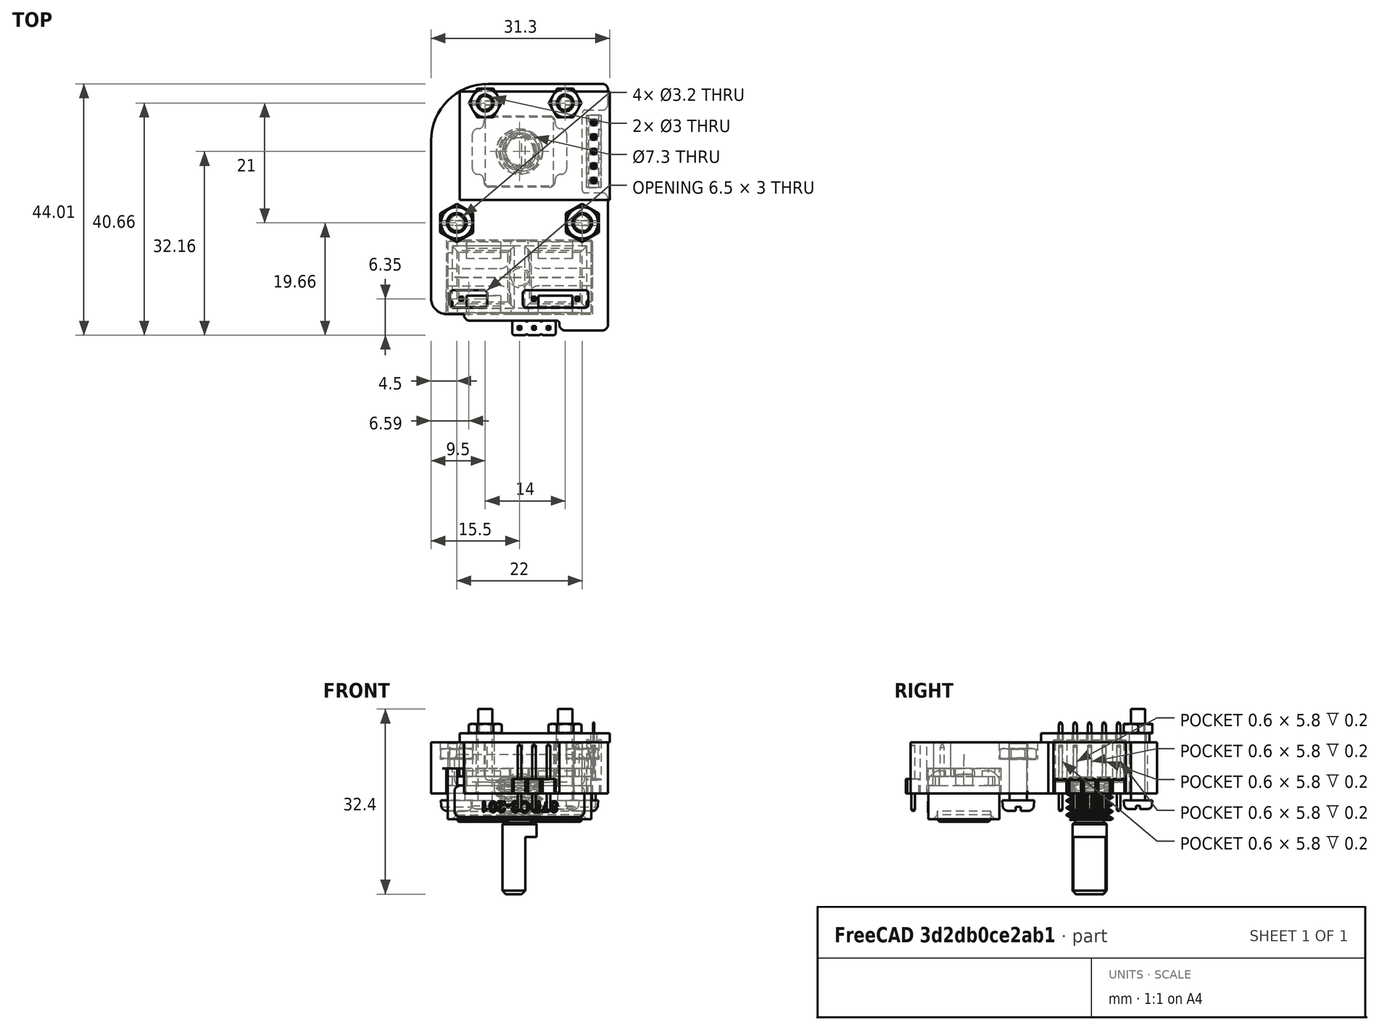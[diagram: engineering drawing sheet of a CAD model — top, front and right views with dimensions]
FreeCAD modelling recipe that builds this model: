
FCSTD DOCUMENT  (FreeCAD 0.18.4R)
Label: MJ_3d_holder_right_3p-r2-asm
License: All rights reserved
LicenseURL: http://en.wikipedia.org/wiki/All_rights_reserved
objects: Sketcher::SketchObject×17, PartDesign::Pad×9, PartDesign::Pocket×8, Part::Feature×8, Part::FeaturePython×8, PartDesign::Fillet×6, PartDesign::Body×6, PartDesign::Chamfer×4, PartDesign::Plane×2, Part::Compound×2, App::DocumentObjectGroup×2, PartDesign::FeatureBase×1, Part::Part2DObjectPython×1, Part::Extrusion×1
note: 90 computed .brp shape members not serialized (recipe doc carries the construction recipe); baked Part::Feature solids carry a one-line shape summary decoded from their .brp

FEATURE [Sketcher::SketchObject] Sketch  label="Sketch_body_outline"
  MapMode = 5
  Support = -> [XY_Plane]
  sketch-geometry (59):
    g0: Circle CenterX=0 CenterY=0 CenterZ=0 NormalX=0 NormalY=0 NormalZ=1 AngleXU=0 Radius=3.65
    g1: Circle CenterX=-11 CenterY=-12.5 CenterZ=0 NormalX=0 NormalY=0 NormalZ=1 AngleXU=0 Radius=1.6
    g2: Circle CenterX=11 CenterY=-12.5 CenterZ=0 NormalX=0 NormalY=0 NormalZ=1 AngleXU=0 Radius=1.6
    g3: Circle CenterX=-6 CenterY=8.5 CenterZ=0 NormalX=0 NormalY=0 NormalZ=1 AngleXU=0 Radius=1.6
    g4: Circle CenterX=8 CenterY=8.5 CenterZ=0 NormalX=0 NormalY=0 NormalZ=1 AngleXU=0 Radius=1.6
    g5: LineSegment [constr] StartX=11 StartY=7.25 StartZ=0 EndX=15 EndY=7.25 EndZ=0
    g6: LineSegment [constr] StartX=15 StartY=7.25 StartZ=0 EndX=15 EndY=-7.25 EndZ=0
    g7: LineSegment [constr] StartX=15 StartY=-7.25 StartZ=0 EndX=11 EndY=-7.25 EndZ=0
    g8: LineSegment [constr] StartX=11 StartY=-7.25 StartZ=0 EndX=11 EndY=7.25 EndZ=0
    g9: GeomPoint X=13 Y=-7.25 Z=0
    g10: GeomPoint X=0 Y=-22 Z=0
    g11: LineSegment [constr] StartX=-12.7 StartY=-15.65 StartZ=0 EndX=12.7 EndY=-15.65 EndZ=0
    g12: LineSegment [constr] StartX=12.7 StartY=-15.65 StartZ=0 EndX=12.7 EndY=-28.35 EndZ=0
    g13: LineSegment [constr] StartX=12.7 StartY=-28.35 StartZ=0 EndX=-12.7 EndY=-28.35 EndZ=0
    g14: LineSegment [constr] StartX=-12.7 StartY=-28.35 StartZ=0 EndX=-12.7 EndY=-15.65 EndZ=0
    g15: LineSegment StartX=15.5 StartY=-31.35 StartZ=0 EndX=15.5 EndY=-7.25 EndZ=0
    g16: LineSegment StartX=15.5 StartY=11.85 StartZ=0 EndX=-5.5 EndY=11.85 EndZ=0
    g17: LineSegment StartX=-15.5 StartY=1.85 StartZ=0 EndX=-15.5 EndY=-25.7 EndZ=0
    g18: LineSegment [constr] StartX=-7 StartY=-29.62 StartZ=0 EndX=7 EndY=-29.62 EndZ=0
    g19: LineSegment [constr] StartX=7 StartY=-29.62 StartZ=0 EndX=7 EndY=-32.16 EndZ=0
    g20: LineSegment [constr] StartX=7 StartY=-32.16 StartZ=0 EndX=-7 EndY=-32.16 EndZ=0
    g21: LineSegment [constr] StartX=-7 StartY=-32.16 StartZ=0 EndX=-7 EndY=-29.62 EndZ=0
    g22: GeomPoint X=-7 Y=-30.89 Z=0
    g23: LineSegment [constr] StartX=-6 StartY=6 StartZ=0 EndX=6 EndY=6 EndZ=0
    g24: LineSegment [constr] StartX=6 StartY=6 StartZ=0 EndX=6 EndY=-6 EndZ=0
    g25: LineSegment [constr] StartX=6 StartY=-6 StartZ=0 EndX=-6 EndY=-6 EndZ=0
    g26: LineSegment [constr] StartX=-6 StartY=-6 StartZ=0 EndX=-6 EndY=6 EndZ=0
    g27: LineSegment [constr] StartX=-10.5 StartY=10.5 StartZ=0 EndX=15.8 EndY=10.5 EndZ=0
    g28: LineSegment [constr] StartX=15.8 StartY=10.5 StartZ=0 EndX=15.8 EndY=-8.5 EndZ=0
    g29: LineSegment [constr] StartX=15.8 StartY=-8.5 StartZ=0 EndX=-10.5 EndY=-8.5 EndZ=0
    g30: LineSegment [constr] StartX=-10.5 StartY=-8.5 StartZ=0 EndX=-10.5 EndY=10.5 EndZ=0
    g31: LineSegment StartX=11 StartY=7.25 StartZ=0 EndX=15.5 EndY=7.25 EndZ=0
    g32: LineSegment StartX=15.5 StartY=-7.25 StartZ=0 EndX=11 EndY=-7.25 EndZ=0
    g33: LineSegment StartX=11 StartY=-7.25 StartZ=0 EndX=11 EndY=7.25 EndZ=0
    g34: LineSegment StartX=15.5 StartY=7.25 StartZ=0 EndX=15.5 EndY=11.85 EndZ=0
    g35: LineSegment StartX=7 StartY=-29.62 StartZ=0 EndX=7 EndY=-31.35 EndZ=0
    g36: LineSegment StartX=7 StartY=-31.35 StartZ=0 EndX=15.5 EndY=-31.35 EndZ=0
    g37: Circle [constr] CenterX=-10.16 CenterY=-25.81 CenterZ=0 NormalX=0 NormalY=0 NormalZ=1 AngleXU=0 Radius=0.5
    g38: Circle [constr] CenterX=2.54 CenterY=-25.81 CenterZ=0 NormalX=0 NormalY=0 NormalZ=1 AngleXU=0 Radius=0.5
    g39: Circle [constr] CenterX=10.16 CenterY=-25.81 CenterZ=0 NormalX=0 NormalY=0 NormalZ=1 AngleXU=0 Radius=0.5
    g40: LineSegment StartX=-5.66 StartY=-24.31 StartZ=0 EndX=-12.16 EndY=-24.31 EndZ=0
    g41: LineSegment StartX=-12.16 StartY=-24.31 StartZ=0 EndX=-12.16 EndY=-27.31 EndZ=0
    g42: LineSegment StartX=-12.16 StartY=-27.31 StartZ=0 EndX=-5.66 EndY=-27.31 EndZ=0
    g43: LineSegment StartX=-5.66 StartY=-27.31 StartZ=0 EndX=-5.66 EndY=-24.31 EndZ=0
    g44: LineSegment StartX=0.6 StartY=-24.31 StartZ=0 EndX=12.1 EndY=-24.31 EndZ=0
    g45: LineSegment StartX=12.1 StartY=-24.31 StartZ=0 EndX=12.1 EndY=-27.31 EndZ=0
    g46: LineSegment StartX=12.1 StartY=-27.31 StartZ=0 EndX=0.6 EndY=-27.31 EndZ=0
    g47: LineSegment StartX=0.6 StartY=-27.31 StartZ=0 EndX=0.6 EndY=-24.31 EndZ=0
    g48: GeomPoint X=6.35 Y=-25.81 Z=0
    g49: ArcOfCircle CenterX=-12.7 CenterY=-25.7 CenterZ=0 NormalX=0 NormalY=0 NormalZ=1 AngleXU=0 Radius=2.8 StartAngle=3.14159 EndAngle=4.71239
    g50: LineSegment StartX=-9.7 StartY=-29.62 StartZ=0 EndX=7 EndY=-29.62 EndZ=0
    g51: LineSegment StartX=-9.7 StartY=-29.62 StartZ=0 EndX=-9.7 EndY=-28.5 EndZ=0
    g52: LineSegment StartX=-9.7 StartY=-28.5 StartZ=0 EndX=-12.7 EndY=-28.5 EndZ=0
    g53: Circle [constr] CenterX=0 CenterY=-30.89 CenterZ=0 NormalX=0 NormalY=0 NormalZ=1 AngleXU=0 Radius=0.5
    g54: Circle [constr] CenterX=2.54 CenterY=-30.89 CenterZ=0 NormalX=0 NormalY=0 NormalZ=1 AngleXU=0 Radius=0.5
    g55: Circle [constr] CenterX=5.08 CenterY=-30.89 CenterZ=0 NormalX=0 NormalY=0 NormalZ=1 AngleXU=0 Radius=0.5
    g56: ArcOfCircle CenterX=-5.5 CenterY=1.85 CenterZ=0 NormalX=0 NormalY=0 NormalZ=1 AngleXU=0 Radius=10 StartAngle=1.5708 EndAngle=3.14159
    g57: GeomPoint X=-15.5 Y=-12.5 Z=0
    g58: GeomPoint X=15.5 Y=-12.5 Z=0
  constraints (157):
    c: Coincident(g0,g-1)
    c: Diameter(g0) = 7.3
    c: Diameter(g2) = 3.2
    c: Equal(g1,g2)
    c: DistanceY(g2,g-1) = 12.5
    c: DistanceX(g1,g2) = 22
    c: Symmetric(g1,g2,g-2)
    c: Horizontal(g3,g4)
    c: Equal(g2,g4)
    c: Equal(g4,g3)
    c: DistanceY(g-1,g3) = 8.5
    c: DistanceX(g3,g4) = 14
    c: DistanceX(g3,g-1) = 6
    c: Coincident(g5,g6)
    c: Coincident(g6,g7)
    c: Coincident(g7,g8)
    c: Coincident(g8,g5)
    c: Horizontal(g5)
    c: Horizontal(g7)
    c: Vertical(g8)
    c: DistanceX(g5,g5) = 4
    c: DistanceY(g6,g6) = 14.5
    c: Symmetric(g5,g6,g-1)
    c: DistanceX(g-1,g9) = 13
    c: Symmetric(g7,g6,g9)
    c: PointOnObject(g10,g-2)
    c: DistanceY(g10,g0) = 22
    c: Coincident(g11,g12)
    c: Coincident(g12,g13)
    c: Coincident(g13,g14)
    c: Coincident(g14,g11)
    c: Horizontal(g11)
    c: Vertical(g12)
    c: Vertical(g14)
    c: DistanceX(g13,g13) = 25.4
    c: DistanceY(g12,g12) = 12.7
    c: Horizontal(g13)
    c: Symmetric(g11,g12,g10)
    c: Coincident(g36,g15)
    c: Coincident(g34,g16)
    c: Vertical(g15)
    c: Vertical(g17)
    c: DistanceY(g36,g12) = 3
    c: Coincident(g18,g19)
    c: Coincident(g19,g20)
    c: Coincident(g20,g21)
    c: Coincident(g21,g18)
    c: Vertical(g19)
    c: Vertical(g21)
    c: DistanceY(g19,g19) = 2.54
    c: DistanceX(g18,g18) = 14
    c: DistanceY(g22,g13) = 2.54
    c: Symmetric(g18,g20,g22)
    c: Coincident(g23,g24)
    c: Coincident(g24,g25)
    c: Coincident(g25,g26)
    c: Coincident(g26,g23)
    c: Horizontal(g23)
    c: Horizontal(g25)
    c: Vertical(g24)
    c: Vertical(g26)
    c: DistanceX(g23,g23) = 12
    c: Equal(g24,g23)
    c: Symmetric(g23,g24,g0)
    c: Coincident(g27,g28)
    c: Coincident(g28,g29)
    c: Coincident(g29,g30)
    c: Coincident(g30,g27)
    c: Horizontal(g27)
    c: Horizontal(g29)
    c: Vertical(g28)
    c: Vertical(g30)
    c: DistanceY(g28,g28) = 19
    c: DistanceX(g27,g27) = 26.3
    c: DistanceX(g27,g-1) = 10.5
    c: DistanceY(g-1,g27) = 10.5
    c: Coincident(g32,g33)
    c: Coincident(g33,g31)
    c: Horizontal(g31)
    c: Horizontal(g32)
    c: Vertical(g33)
    c: Coincident(g31,g5)
    c: Equal(g6,g33)
    c: Tangent(g15,g34)
    c: Vertical(g35)
    c: PointOnObject(g36,g19)
    c: Coincident(g32,g15)
    c: Coincident(g31,g34)
    c: Horizontal(g39,g38)
    c: Horizontal(g38,g37)
    c: Equal(g39,g38)
    c: Equal(g38,g37)
    c: Diameter(g37) = 1
    c: DistanceY(g37,g10) = 3.81
    c: DistanceX(g38,g39) = 7.62
    c: DistanceX(g10,g38) = 2.54
    c: DistanceX(g37,g-1) = 10.16
    c: Coincident(g40,g41)
    c: Coincident(g41,g42)
    c: Coincident(g42,g43)
    c: Coincident(g43,g40)
    c: Horizontal(g40)
    c: Horizontal(g42)
    c: Vertical(g41)
    c: Vertical(g43)
    c: Coincident(g44,g45)
    c: Coincident(g45,g46)
    c: Coincident(g46,g47)
    c: Coincident(g47,g44)
    c: Horizontal(g44)
    c: Horizontal(g46)
    c: Vertical(g45)
    c: Vertical(g47)
    c: Equal(g47,g43)
    c: DistanceY(g45,g45) = 3
    c: Symmetric(g38,g39,g48)
    c: Symmetric(g44,g45,g48)
    c: Horizontal(g44,g40)
    c: DistanceX(g46,g46) = 11.5
    c: DistanceX(g42,g42) = 6.5
    c: DistanceX(g40,g37) = 2
    c: DistanceY(g34,g34) = 4.6
    c: Tangent(g17,g49) = -1.5708
    c: Horizontal(g35,g18)
    c: Coincident(g35,g36)
    c: Symmetric(g20,g19,g-2)
    c: Horizontal(g18)
    c: PointOnObject(g50,g18)
    c: Coincident(g50,g35)
    c: Horizontal(g36)
    c: Vertical(g49,g49)
    c: Coincident(g51,g50)
    c: Vertical(g51)
    c: DistanceY(g51,g51) = 1.12
    c: Coincident(g52,g51)
    c: Horizontal(g52)
    c: DistanceX(g52,g52) = 3
    c: Coincident(g49,g52)
    c: Radius(g49) = 2.8
    c: PointOnObject(g53,g-2)
    c: Equal(g38,g53)
    c: Equal(g53,g54)
    c: Equal(g54,g55)
    c: Horizontal(g53,g54)
    c: Horizontal(g54,g55)
    c: DistanceX(g53,g54) = 2.54
    c: DistanceX(g54,g55) = 2.54
    c: DistanceY(g54,g38) = 5.08
    c: DistanceX(g17,g15) = 31
    c: Tangent(g17,g56) = -1.5708
    c: Tangent(g16,g56) = -1.5708
    c: Radius(g56) = 10
    c: Horizontal(g16)
    c: PointOnObject(g57,g17)
    c: PointOnObject(g58,g15)
    c: Horizontal(g2,g58)
    c: Symmetric(g57,g58,g-2)
FEATURE [PartDesign::Pad] Pad  label="BodyPad"
  Length = 9
  Length2 = 100
  Profile = -> Sketch
  Type = 0
FEATURE [Sketcher::SketchObject] Sketch002  label="Sketch_rotary_7mm_pocket"
  MapMode = 5
  Placement = pos=(0,0,9) rot=(0,0,1;0rad)
  Support = -> [Pad]
  sketch-geometry (12):
    g0: LineSegment StartX=8.25 StartY=-4 StartZ=0 EndX=6.25 EndY=-4 EndZ=0
    g1: LineSegment StartX=-8.25 StartY=-4 StartZ=0 EndX=-8.25 EndY=4 EndZ=0
    g2: LineSegment StartX=-8.25 StartY=4 StartZ=0 EndX=-6.25 EndY=4 EndZ=0
    g3: LineSegment StartX=8.25 StartY=4 StartZ=0 EndX=8.25 EndY=-4 EndZ=0
    g4: LineSegment StartX=-6.25 StartY=6.25 StartZ=0 EndX=6.25 EndY=6.25 EndZ=0
    g5: LineSegment StartX=6.25 StartY=6.25 StartZ=0 EndX=6.25 EndY=4 EndZ=0
    g6: LineSegment StartX=6.25 StartY=-6.25 StartZ=0 EndX=-6.25 EndY=-6.25 EndZ=0
    g7: LineSegment StartX=-6.25 StartY=-6.25 StartZ=0 EndX=-6.25 EndY=-4 EndZ=0
    g8: LineSegment StartX=6.25 StartY=4 StartZ=0 EndX=8.25 EndY=4 EndZ=0
    g9: LineSegment StartX=-6.25 StartY=-4 StartZ=0 EndX=-8.25 EndY=-4 EndZ=0
    g10: LineSegment StartX=-6.25 StartY=4 StartZ=0 EndX=-6.25 EndY=6.25 EndZ=0
    g11: LineSegment StartX=6.25 StartY=-4 StartZ=0 EndX=6.25 EndY=-6.25 EndZ=0
  constraints (30):
    c: Coincident(g9,g1)
    c: Coincident(g1,g2)
    c: Coincident(g8,g3)
    c: Coincident(g3,g0)
    c: Horizontal(g0)
    c: Horizontal(g2)
    c: Vertical(g1)
    c: Vertical(g3)
    c: DistanceX(g2,g8) = 16.5
    c: DistanceY(g1,g1) = 8
    c: Symmetric(g0,g1,g-1)
    c: Coincident(g4,g5)
    c: Coincident(g11,g6)
    c: Coincident(g6,g7)
    c: Coincident(g10,g4)
    c: Horizontal(g4)
    c: Horizontal(g6)
    c: Vertical(g5)
    c: Vertical(g7)
    c: DistanceX(g4,g4) = 12.5
    c: DistanceY(g7,g10) = 12.5
    c: Symmetric(g4,g11,g-1)
    c: Tangent(g2,g8)
    c: Tangent(g0,g9)
    c: Coincident(g7,g9)
    c: Coincident(g10,g2)
    c: Tangent(g7,g10)
    c: Coincident(g5,g8)
    c: Coincident(g11,g0)
    c: Tangent(g5,g11)
FEATURE [PartDesign::Pocket] Pocket  label="RotaryPocket"
  BaseFeature = -> Pad
  Length = 7
  Length2 = 100
  Profile = -> Sketch002
  Type = 0
FEATURE [Sketcher::SketchObject] Sketch001  label="Sketch_hexnut_3mm_pockets"
  MapMode = 5
  Placement = pos=(0,0,9) rot=(0,0,1;0rad)
  Support = -> [Pocket]
  sketch-geometry (14):
    g0: LineSegment StartX=-8.1 StartY=-14.1743 StartZ=0 EndX=-8.1 EndY=-10.8257 EndZ=0
    g1: LineSegment StartX=-8.1 StartY=-10.8257 StartZ=0 EndX=-11 EndY=-9.15137 EndZ=0
    g2: LineSegment StartX=-11 StartY=-9.15137 StartZ=0 EndX=-13.9 EndY=-10.8257 EndZ=0
    g3: LineSegment StartX=-13.9 StartY=-10.8257 StartZ=0 EndX=-13.9 EndY=-14.1743 EndZ=0
    g4: LineSegment StartX=-13.9 StartY=-14.1743 StartZ=0 EndX=-11 EndY=-15.8486 EndZ=0
    g5: LineSegment StartX=-11 StartY=-15.8486 StartZ=0 EndX=-8.1 EndY=-14.1743 EndZ=0
    g6: Circle [constr] CenterX=-11 CenterY=-12.5 CenterZ=0 NormalX=0 NormalY=0 NormalZ=1 AngleXU=0 Radius=3.34863
    g7: LineSegment StartX=13.9 StartY=-14.1743 StartZ=0 EndX=13.9 EndY=-10.8257 EndZ=0
    g8: LineSegment StartX=13.9 StartY=-10.8257 StartZ=0 EndX=11 EndY=-9.15137 EndZ=0
    g9: LineSegment StartX=11 StartY=-9.15137 StartZ=0 EndX=8.1 EndY=-10.8257 EndZ=0
    g10: LineSegment StartX=8.1 StartY=-10.8257 StartZ=0 EndX=8.1 EndY=-14.1743 EndZ=0
    g11: LineSegment StartX=8.1 StartY=-14.1743 StartZ=0 EndX=11 EndY=-15.8486 EndZ=0
    g12: LineSegment StartX=11 StartY=-15.8486 StartZ=0 EndX=13.9 EndY=-14.1743 EndZ=0
    g13: Circle [constr] CenterX=11 CenterY=-12.5 CenterZ=0 NormalX=0 NormalY=0 NormalZ=1 AngleXU=0 Radius=3.34863
  constraints (33):
    c: Coincident(g0,g1)
    c: Coincident(g1,g2)
    c: Coincident(g2,g3)
    c: Coincident(g3,g4)
    c: Coincident(g4,g5)
    c: Coincident(g5,g0)
    c: Equal(g0, g1-g5) x5
    c: PointOnObject(g0,g6)
    c: PointOnObject(g1,g6)
    c: PointOnObject(g2,g6)
    c: PointOnObject(g3,g6)
    c: PointOnObject(g4,g6)
    c: PointOnObject(g5,g6)
    c: Coincident(g7,g8)
    c: Coincident(g8,g9)
    c: Coincident(g9,g10)
    c: Coincident(g10,g11)
    c: Coincident(g11,g12)
    c: Coincident(g12,g7)
    c: Equal(g7, g8-g12) x5
    c: PointOnObject(g7,g13)
    c: PointOnObject(g8,g13)
    c: PointOnObject(g9,g13)
    c: PointOnObject(g10,g13)
    c: PointOnObject(g11,g13)
    c: PointOnObject(g12,g13)
    c: DistanceX(g6,g13) = 22
    c: Symmetric(g6,g13,g-2)
    c: DistanceY(g6,g-1) = 12.5
    c: DistanceX(g3,g0) = 5.8
    c: Vertical(g3)
    c: DistanceX(g10,g7) = 5.8
    c: Vertical(g7)
FEATURE [PartDesign::Pocket] Pocket001
  BaseFeature = -> Pocket
  Length = 3
  Length2 = 100
  Profile = -> Sketch001
  Type = 0
FEATURE [Sketcher::SketchObject] Sketch003  label="Sketch_Grayhill_3mm_pocket"
  MapMode = 5
  Placement = pos=(0,0,0) rot=(1,0,0;3.14159rad)
  Support = -> [Pocket001]
  sketch-geometry (5):
    g0: LineSegment StartX=12.85 StartY=15.5 StartZ=0 EndX=-12.85 EndY=15.5 EndZ=0
    g1: LineSegment StartX=-12.85 StartY=15.5 StartZ=0 EndX=-12.85 EndY=28.5 EndZ=0
    g2: LineSegment StartX=-12.85 StartY=28.5 StartZ=0 EndX=12.85 EndY=28.5 EndZ=0
    g3: LineSegment StartX=12.85 StartY=28.5 StartZ=0 EndX=12.85 EndY=15.5 EndZ=0
    g4: GeomPoint X=0 Y=22 Z=0
  constraints (13):
    c: Coincident(g0,g1)
    c: Coincident(g1,g2)
    c: Coincident(g2,g3)
    c: Coincident(g3,g0)
    c: Horizontal(g0)
    c: Horizontal(g2)
    c: Vertical(g1)
    c: Vertical(g3)
    c: DistanceX(g2,g2) = 25.7
    c: DistanceY(g3,g3) = 13
    c: PointOnObject(g4,g-2)
    c: DistanceY(g-1,g4) = 22
    c: Symmetric(g0,g1,g4)
FEATURE [PartDesign::Pocket] Pocket002
  BaseFeature = -> Pocket001
  Length = 3
  Length2 = 100
  Profile = -> Sketch003
  Type = 0
FEATURE [Sketcher::SketchObject] Sketch004  label="Sketch_Grayhill_1_4mm_pocket"
  MapMode = 5
  Placement = pos=(0,0,3) rot=(1,0,0;3.14159rad)
  Support = -> [Pocket002]
  sketch-geometry (34):
    g0: LineSegment [constr] StartX=12.85 StartY=15.5 StartZ=0 EndX=-12.85 EndY=15.5 EndZ=0
    g1: LineSegment [constr] StartX=-12.85 StartY=15.5 StartZ=0 EndX=-12.85 EndY=28.5 EndZ=0
    g2: LineSegment [constr] StartX=-12.85 StartY=28.5 StartZ=0 EndX=12.85 EndY=28.5 EndZ=0
    g3: LineSegment [constr] StartX=12.85 StartY=28.5 StartZ=0 EndX=12.85 EndY=15.5 EndZ=0
    g4: GeomPoint X=0 Y=22 Z=0
    g5: LineSegment [constr] StartX=12.85 StartY=20.5 StartZ=0 EndX=-12.85 EndY=20.5 EndZ=0
    g6: LineSegment [constr] StartX=-12.85 StartY=20.5 StartZ=0 EndX=-12.85 EndY=23.5 EndZ=0
    g7: LineSegment [constr] StartX=-12.85 StartY=23.5 StartZ=0 EndX=12.85 EndY=23.5 EndZ=0
    g8: LineSegment [constr] StartX=12.85 StartY=23.5 StartZ=0 EndX=12.85 EndY=20.5 EndZ=0
    g9: LineSegment [constr] StartX=1.5 StartY=15.5 StartZ=0 EndX=-1.5 EndY=15.5 EndZ=0
    g10: LineSegment [constr] StartX=-1.5 StartY=15.5 StartZ=0 EndX=-1.5 EndY=28.5 EndZ=0
    g11: LineSegment [constr] StartX=-1.5 StartY=28.5 StartZ=0 EndX=1.5 EndY=28.5 EndZ=0
    g12: LineSegment [constr] StartX=1.5 StartY=28.5 StartZ=0 EndX=1.5 EndY=15.5 EndZ=0
    g13: Circle CenterX=0 CenterY=22 CenterZ=0 NormalX=0 NormalY=0 NormalZ=1 AngleXU=0 Radius=1.8
    g14: LineSegment StartX=1.5 StartY=15.5 StartZ=0 EndX=12.85 EndY=15.5 EndZ=0
    g15: LineSegment StartX=12.85 StartY=15.5 StartZ=0 EndX=12.85 EndY=20.5 EndZ=0
    g16: LineSegment StartX=12.85 StartY=20.5 StartZ=0 EndX=3.5 EndY=20.5 EndZ=0
    g17: LineSegment StartX=1.5 StartY=18.5 StartZ=0 EndX=1.5 EndY=15.5 EndZ=0
    g18: LineSegment StartX=-1.5 StartY=15.5 StartZ=0 EndX=-12.85 EndY=15.5 EndZ=0
    g19: LineSegment StartX=-12.85 StartY=15.5 StartZ=0 EndX=-12.85 EndY=20.5 EndZ=0
    g20: LineSegment StartX=-12.85 StartY=20.5 StartZ=0 EndX=-3.5 EndY=20.5 EndZ=0
    g21: LineSegment StartX=-1.5 StartY=18.5 StartZ=0 EndX=-1.5 EndY=15.5 EndZ=0
    g22: LineSegment StartX=12.85 StartY=23.5 StartZ=0 EndX=3.5 EndY=23.5 EndZ=0
    g23: LineSegment StartX=1.5 StartY=25.5 StartZ=0 EndX=1.5 EndY=28.5 EndZ=0
    g24: LineSegment StartX=1.5 StartY=28.5 StartZ=0 EndX=12.85 EndY=28.5 EndZ=0
    g25: LineSegment StartX=12.85 StartY=28.5 StartZ=0 EndX=12.85 EndY=23.5 EndZ=0
    g26: LineSegment StartX=-12.85 StartY=23.5 StartZ=0 EndX=-3.5 EndY=23.5 EndZ=0
    g27: LineSegment StartX=-1.5 StartY=25.5 StartZ=0 EndX=-1.5 EndY=28.5 EndZ=0
    g28: LineSegment StartX=-1.5 StartY=28.5 StartZ=0 EndX=-12.85 EndY=28.5 EndZ=0
    g29: LineSegment StartX=-12.85 StartY=28.5 StartZ=0 EndX=-12.85 EndY=23.5 EndZ=0
    g30: ArcOfCircle CenterX=3.5 CenterY=18.5 CenterZ=0 NormalX=0 NormalY=0 NormalZ=1 AngleXU=0 Radius=2 StartAngle=1.5708 EndAngle=3.14159
    g31: ArcOfCircle CenterX=-3.5 CenterY=18.5 CenterZ=0 NormalX=0 NormalY=0 NormalZ=1 AngleXU=0 Radius=2 StartAngle=-9e-16 EndAngle=1.5708
    g32: ArcOfCircle CenterX=-3.5 CenterY=25.5 CenterZ=0 NormalX=0 NormalY=0 NormalZ=1 AngleXU=0 Radius=2 StartAngle=4.71239 EndAngle=6.28319
    g33: ArcOfCircle CenterX=3.5 CenterY=25.5 CenterZ=0 NormalX=0 NormalY=0 NormalZ=1 AngleXU=0 Radius=2 StartAngle=3.14159 EndAngle=4.71239
  constraints (85):
    c: Coincident(g0,g1)
    c: Coincident(g1,g2)
    c: Coincident(g2,g3)
    c: Coincident(g3,g0)
    c: Horizontal(g0)
    c: Horizontal(g2)
    c: Vertical(g1)
    c: Vertical(g3)
    c: DistanceX(g0,g0) = 25.7
    c: DistanceY(g3,g3) = 13
    c: PointOnObject(g4,g-2)
    c: DistanceY(g-1,g4) = 22
    c: Symmetric(g0,g1,g4)
    c: Coincident(g5,g6)
    c: Coincident(g6,g7)
    c: Coincident(g7,g8)
    c: Coincident(g8,g5)
    c: Horizontal(g5)
    c: Horizontal(g7)
    c: Vertical(g6)
    c: Vertical(g8)
    c: PointOnObject(g5,g3)
    c: Symmetric(g5,g6,g4)
    c: DistanceY(g5,g7) = 3
    c: Coincident(g9,g10)
    c: Coincident(g10,g11)
    c: Coincident(g11,g12)
    c: Coincident(g12,g9)
    c: Horizontal(g9)
    c: Horizontal(g11)
    c: Vertical(g10)
    c: Vertical(g12)
    c: PointOnObject(g9,g0)
    c: Symmetric(g9,g10,g4)
    c: DistanceX(g10,g11) = 3
    c: Coincident(g13,g4)
    c: Diameter(g13) = 3.6
    c: Coincident(g14,g15)
    c: Coincident(g15,g16)
    c: Coincident(g17,g14)
    c: Horizontal(g14)
    c: Horizontal(g16)
    c: Vertical(g15)
    c: Vertical(g17)
    c: Coincident(g14,g9)
    c: Coincident(g15,g5)
    c: Coincident(g18,g19)
    c: Coincident(g19,g20)
    c: Coincident(g21,g18)
    c: Horizontal(g18)
    c: Horizontal(g20)
    c: Vertical(g19)
    c: Vertical(g21)
    c: Coincident(g18,g9)
    c: Coincident(g19,g5)
    c: Coincident(g23,g24)
    c: Coincident(g24,g25)
    c: Coincident(g25,g22)
    c: Horizontal(g22)
    c: Horizontal(g24)
    c: Vertical(g23)
    c: Vertical(g25)
    c: Coincident(g22,g7)
    c: Coincident(g23,g11)
    c: Coincident(g27,g28)
    c: Coincident(g28,g29)
    c: Coincident(g29,g26)
    c: Horizontal(g26)
    c: Horizontal(g28)
    c: Vertical(g27)
    c: Vertical(g29)
    c: Coincident(g26,g6)
    c: Coincident(g27,g10)
    c: Tangent(g17,g30) = -1.5708
    c: Tangent(g16,g30) = -1.5708
    c: Tangent(g21,g31) = 1.5708
    c: Tangent(g20,g31) = 1.5708
    c: Tangent(g26,g32) = -1.5708
    c: Tangent(g27,g32) = -1.5708
    c: Tangent(g22,g33) = 1.5708
    c: Tangent(g23,g33) = 1.5708
    c: Radius(g30) = 2
    c: Equal(g30,g31)
    c: Equal(g31,g32)
    c: Equal(g32,g33)
FEATURE [PartDesign::Pocket] Pocket003
  BaseFeature = -> Pocket002
  Length = 1.4
  Length2 = 100
  Profile = -> Sketch004
  Type = 0
FEATURE [PartDesign::Fillet] Fillet
  Base = -> Pocket003 [Edge85,Edge10,Edge1,Edge107,Edge104,Edge103]
  BaseFeature = -> Pocket003
  Radius = 1
FEATURE [PartDesign::Fillet] Fillet001
  Base = -> Fillet [Edge151,Edge147,Edge143,Edge135,Edge149,Edge153,Edge145,Edge133,Edge137,Edge141,Edge132,Edge139]
  BaseFeature = -> Fillet
  Radius = 0.99
FEATURE [PartDesign::Fillet] Fillet002
  Base = -> Fillet001 [Edge153,Edge150,Edge117,Edge281,Edge284,Edge269,Edge173,Edge267,Edge230,Edge170,Edge176,Edge180,Edge166,Edge175,Edge165,Edge285,Edge256,Edge168,Edge178,Edge214,Edge215,Edge161,Edge163,Edge133]
  BaseFeature = -> Fillet001
  Radius = 0.5
FEATURE [PartDesign::Body] Body  label="3d_holder_right-r2"
  Group = -> [Sketch004,Sketch,Pad,Sketch001,Sketch002,Sketch003,Pocket,Pocket001,Pocket002,Pocket003,Fillet,Fillet001,Fillet002]
  Origin = -> Origin
  Tip = -> Fillet002
FEATURE [Sketcher::SketchObject] Sketch012
  MapMode = 5
  Placement = pos=(0,0,0) rot=(1,0,0;1.5708rad)
  Support = -> [XZ_Plane003]
  sketch-geometry (12):
    g0: LineSegment StartX=-11.725 StartY=5.425 StartZ=0 EndX=11.725 EndY=5.425 EndZ=0
    g1: LineSegment StartX=11.725 StartY=5.425 StartZ=0 EndX=11.725 EndY=4.275 EndZ=0
    g2: LineSegment StartX=11.725 StartY=4.275 StartZ=0 EndX=12.575 EndY=4.275 EndZ=0
    g3: LineSegment StartX=12.575 StartY=4.275 StartZ=0 EndX=12.575 EndY=-4.275 EndZ=0
    g4: LineSegment StartX=12.575 StartY=-4.275 StartZ=0 EndX=11.725 EndY=-4.275 EndZ=0
    g5: LineSegment StartX=11.725 StartY=-4.275 StartZ=0 EndX=11.725 EndY=-5.425 EndZ=0
    g6: LineSegment StartX=11.725 StartY=-5.425 StartZ=0 EndX=-11.725 EndY=-5.425 EndZ=0
    g7: LineSegment StartX=-11.725 StartY=-5.425 StartZ=0 EndX=-11.725 EndY=-4.275 EndZ=0
    g8: LineSegment StartX=-11.725 StartY=-4.275 StartZ=0 EndX=-12.575 EndY=-4.275 EndZ=0
    g9: LineSegment StartX=-12.575 StartY=-4.275 StartZ=0 EndX=-12.575 EndY=4.275 EndZ=0
    g10: LineSegment StartX=-12.575 StartY=4.275 StartZ=0 EndX=-11.725 EndY=4.275 EndZ=0
    g11: LineSegment StartX=-11.725 StartY=4.275 StartZ=0 EndX=-11.725 EndY=5.425 EndZ=0
  constraints (34):
    c: Horizontal(g0)
    c: Coincident(g0,g1)
    c: Vertical(g1)
    c: Coincident(g1,g2)
    c: Horizontal(g2)
    c: Coincident(g2,g3)
    c: Vertical(g3)
    c: Coincident(g3,g4)
    c: Horizontal(g4)
    c: Coincident(g4,g5)
    c: Vertical(g5)
    c: Coincident(g5,g6)
    c: Coincident(g6,g7)
    c: Vertical(g7)
    c: Coincident(g7,g8)
    c: Horizontal(g8)
    c: Coincident(g8,g9)
    c: Coincident(g9,g10)
    c: Coincident(g10,g11)
    c: Coincident(g11,g0)
    c: Equal(g11,g1)
    c: Equal(g1,g5)
    c: Equal(g5,g7)
    c: Equal(g2,g4)
    c: Equal(g4,g8)
    c: Equal(g8,g10)
    c: Equal(g3,g9)
    c: Equal(g0,g6)
    c: DistanceX(g9,g2) = 25.15
    c: DistanceY(g5,g0) = 10.85
    c: DistanceX(g10,g10) = 0.85
    c: DistanceY(g11,g11) = 1.15
    c: Symmetric(g6,g6,g-2)
    c: Symmetric(g9,g9,g-1)
FEATURE [PartDesign::Pad] Pad008  label="PCBPad"
  Length = 1.6
  Length2 = 100
  Placement = pos=(0,0,0) rot=(1,0,0;1.5708rad)
  Profile = -> Sketch012
  Reversed = true
  Type = 0
FEATURE [Part::Feature] Part__Feature001  label="BTN_A-Brass_pin-5.75mm"
  Placement = pos=(12.7,0,0) rot=(0,0,1;0rad)
  shape: bbox 0.7 x 5.75 x 0.7 mm, 14 faces (baked)
FEATURE [Sketcher::SketchObject] Sketch013
  MapMode = 5
  Placement = pos=(0,0,0) rot=(1,0,0;1.5708rad)
  Support = -> [XZ_Plane004]
  sketch-geometry (4):
    g0: LineSegment StartX=-12.575 StartY=6.225 StartZ=0 EndX=12.575 EndY=6.225 EndZ=0
    g1: LineSegment StartX=12.575 StartY=6.225 StartZ=0 EndX=12.575 EndY=-6.225 EndZ=0
    g2: LineSegment StartX=12.575 StartY=-6.225 StartZ=0 EndX=-12.575 EndY=-6.225 EndZ=0
    g3: LineSegment StartX=-12.575 StartY=-6.225 StartZ=0 EndX=-12.575 EndY=6.225 EndZ=0
  constraints (10):
    c: Coincident(g0,g1)
    c: Coincident(g1,g2)
    c: Coincident(g2,g3)
    c: Coincident(g3,g0)
    c: Horizontal(g2)
    c: Vertical(g1)
    c: DistanceX(g0,g0) = 25.15
    c: DistanceY(g3,g3) = 12.45
    c: Symmetric(g0,g0,g-2)
    c: Symmetric(g2,g0,g-1)
FEATURE [PartDesign::Pad] Pad001
  Length = 5.9
  Length2 = 100
  Placement = pos=(0,0,0) rot=(1,0,0;1.5708rad)
  Profile = -> Sketch013
  Type = 0
FEATURE [Sketcher::SketchObject] Sketch018
  MapMode = 5
  Placement = pos=(0,-5.9,1.3e-15) rot=(1,0,0;1.5708rad)
  Support = -> [Pad001]
  sketch-geometry (11):
    g0: LineSegment StartX=-11 StartY=4.65 StartZ=0 EndX=-1.7 EndY=4.65 EndZ=0
    g1: LineSegment StartX=-1.7 StartY=4.65 StartZ=0 EndX=-1.7 EndY=-4.65 EndZ=0
    g2: LineSegment StartX=-1.7 StartY=-4.65 StartZ=0 EndX=-11 EndY=-4.65 EndZ=0
    g3: LineSegment StartX=-11 StartY=-4.65 StartZ=0 EndX=-11 EndY=4.65 EndZ=0
    g4: LineSegment [constr] StartX=-6.35 StartY=4.65 StartZ=0 EndX=-6.35 EndY=-4.65 EndZ=0
    g5: LineSegment StartX=1.7 StartY=4.65 StartZ=0 EndX=11 EndY=4.65 EndZ=0
    g6: LineSegment StartX=11 StartY=4.65 StartZ=0 EndX=11 EndY=-4.65 EndZ=0
    g7: LineSegment StartX=11 StartY=-4.65 StartZ=0 EndX=1.7 EndY=-4.65 EndZ=0
    g8: LineSegment StartX=1.7 StartY=-4.65 StartZ=0 EndX=1.7 EndY=4.65 EndZ=0
    g9: LineSegment [constr] StartX=6.35 StartY=4.65 StartZ=0 EndX=6.35 EndY=-4.65 EndZ=0
    g10: LineSegment [constr] StartX=-11 StartY=4.65 StartZ=0 EndX=1.7 EndY=4.65 EndZ=0
  constraints (31):
    c: Coincident(g0,g1)
    c: Coincident(g1,g2)
    c: Coincident(g2,g3)
    c: Coincident(g3,g0)
    c: Horizontal(g0)
    c: Horizontal(g2)
    c: Vertical(g1)
    c: DistanceY(g3,g3) = 9.3
    c: DistanceX(g0,g0) = 9.3
    c: Symmetric(g0,g2,g-1)
    c: PointOnObject(g4,g0)
    c: PointOnObject(g4,g2)
    c: Symmetric(g0,g0,g4)
    c: DistanceX(g4,g-1) = 6.35
    c: Coincident(g5,g6)
    c: Coincident(g6,g7)
    c: Coincident(g7,g8)
    c: Coincident(g8,g5)
    c: Horizontal(g5)
    c: Horizontal(g7)
    c: Vertical(g6)
    c: Equal(g3,g8) = 9.3
    c: Equal(g0,g5) = 9.3
    c: PointOnObject(g9,g5)
    c: PointOnObject(g9,g7)
    c: Symmetric(g5,g5,g9)
    c: Coincident(g0,g10)
    c: Coincident(g5,g10)
    c: Distance(g10) = 12.7
    c: Horizontal(g10)
    c: Vertical(g8)
FEATURE [PartDesign::Pocket] Pocket008
  BaseFeature = -> Pad001
  Length = 1.4
  Length2 = 100
  Placement = pos=(0,0,0) rot=(1,0,0;1.5708rad)
  Profile = -> Sketch018
  Type = 0
FEATURE [PartDesign::Chamfer] Chamfer
  Base = -> Pocket008 [Edge17,Edge20,Edge19,Edge18,Edge16,Edge13,Edge14,Edge15]
  BaseFeature = -> Pocket008
  Placement = pos=(0,0,0) rot=(1,0,0;1.5708rad)
  Size = 0.8
FEATURE [PartDesign::Plane] DatumPlane
  Length = 29.6355
  MapMode = 5
  Placement = pos=(0,-4.5,3.4e-15) rot=(1,0,0;1.5708rad)
  ResizeMode = 0
  Support = -> [Chamfer]
  Width = 24.4855
FEATURE [Sketcher::SketchObject] Sketch011  label="SketchRightBtn"
  MapMode = 5
  Placement = pos=(0,-4.5,3.4e-15) rot=(1,0,0;1.5708rad)
  Support = -> [DatumPlane]
  sketch-geometry (5):
    g0: LineSegment StartX=1.7 StartY=4.65 StartZ=0 EndX=11 EndY=4.65 EndZ=0
    g1: LineSegment StartX=11 StartY=4.65 StartZ=0 EndX=11 EndY=-4.65 EndZ=0
    g2: LineSegment StartX=11 StartY=-4.65 StartZ=0 EndX=1.7 EndY=-4.65 EndZ=0
    g3: LineSegment StartX=1.7 StartY=-4.65 StartZ=0 EndX=1.7 EndY=4.65 EndZ=0
    g4: LineSegment [constr] StartX=6.35 StartY=4.65 StartZ=0 EndX=6.35 EndY=-4.65 EndZ=0
  constraints (14):
    c: Coincident(g0,g1)
    c: Coincident(g1,g2)
    c: Coincident(g2,g3)
    c: Coincident(g3,g0)
    c: Horizontal(g0)
    c: Horizontal(g2)
    c: Vertical(g1)
    c: DistanceY(g3,g3) = 9.3
    c: DistanceX(g0,g0) = 9.3
    c: Symmetric(g0,g2,g-1)
    c: PointOnObject(g4,g0)
    c: PointOnObject(g4,g2)
    c: Symmetric(g0,g0,g4)
    c: DistanceX(g4,g-1) = -6.35
FEATURE [PartDesign::Pad] Pad002
  Length = 1.8
  Length2 = 100
  Placement = pos=(0,-4.5,5e-15) rot=(1,0,0;1.5708rad)
  Profile = -> Sketch011
  Type = 0
FEATURE [Sketcher::SketchObject] Sketch015
  ExternalGeometry = -> [Chamfer]
  MapMode = 5
  Placement = pos=(0,0,0) rot=(-1,0,0;1.5708rad)
  Support = -> [Chamfer]
  sketch-geometry (24):
    g0: LineSegment StartX=12.575 StartY=-4.315 StartZ=0 EndX=12.575 EndY=-6.225 EndZ=0
    g1: LineSegment StartX=12.575 StartY=-6.225 StartZ=0 EndX=10.945 EndY=-6.225 EndZ=0
    g2: LineSegment StartX=10.945 StartY=-6.225 StartZ=0 EndX=10.945 EndY=-5.425 EndZ=0
    g3: LineSegment StartX=10.945 StartY=-5.425 StartZ=0 EndX=11.775 EndY=-5.425 EndZ=0
    g4: LineSegment StartX=11.775 StartY=-5.425 StartZ=0 EndX=11.775 EndY=-4.315 EndZ=0
    g5: LineSegment StartX=11.775 StartY=-4.315 StartZ=0 EndX=12.575 EndY=-4.315 EndZ=0
    g6: LineSegment StartX=-10.945 StartY=-6.225 StartZ=0 EndX=-12.575 EndY=-6.225 EndZ=0
    g7: LineSegment StartX=-12.575 StartY=-6.225 StartZ=0 EndX=-12.575 EndY=-4.315 EndZ=0
    g8: LineSegment StartX=-12.575 StartY=-4.315 StartZ=0 EndX=-11.775 EndY=-4.315 EndZ=0
    g9: LineSegment StartX=-11.775 StartY=-4.315 StartZ=0 EndX=-11.775 EndY=-5.425 EndZ=0
    g10: LineSegment StartX=-11.775 StartY=-5.425 StartZ=0 EndX=-10.945 EndY=-5.425 EndZ=0
    g11: LineSegment StartX=-10.945 StartY=-5.425 StartZ=0 EndX=-10.945 EndY=-6.225 EndZ=0
    g12: LineSegment StartX=12.575 StartY=4.315 StartZ=0 EndX=12.575 EndY=6.225 EndZ=0
    g13: LineSegment StartX=12.575 StartY=6.225 StartZ=0 EndX=10.945 EndY=6.225 EndZ=0
    g14: LineSegment StartX=10.945 StartY=6.225 StartZ=0 EndX=10.945 EndY=5.425 EndZ=0
    g15: LineSegment StartX=10.945 StartY=5.425 StartZ=0 EndX=11.775 EndY=5.425 EndZ=0
    g16: LineSegment StartX=11.775 StartY=5.425 StartZ=0 EndX=11.775 EndY=4.315 EndZ=0
    g17: LineSegment StartX=11.775 StartY=4.315 StartZ=0 EndX=12.575 EndY=4.315 EndZ=0
    g18: LineSegment StartX=-11.775 StartY=4.315 StartZ=0 EndX=-11.775 EndY=5.425 EndZ=0
    g19: LineSegment StartX=-11.775 StartY=5.425 StartZ=0 EndX=-10.945 EndY=5.425 EndZ=0
    g20: LineSegment StartX=-10.945 StartY=5.425 StartZ=0 EndX=-10.945 EndY=6.225 EndZ=0
    g21: LineSegment StartX=-10.945 StartY=6.225 StartZ=0 EndX=-12.575 EndY=6.225 EndZ=0
    g22: LineSegment StartX=-12.575 StartY=6.225 StartZ=0 EndX=-12.575 EndY=4.315 EndZ=0
    g23: LineSegment StartX=-12.575 StartY=4.315 StartZ=0 EndX=-11.775 EndY=4.315 EndZ=0
  constraints (68):
    c: Vertical(g0)
    c: Coincident(g0,g1)
    c: Horizontal(g1)
    c: Coincident(g1,g2)
    c: Vertical(g2)
    c: Coincident(g2,g3)
    c: Horizontal(g3)
    c: Coincident(g3,g4)
    c: Vertical(g4)
    c: Coincident(g4,g5)
    c: Coincident(g5,g0)
    c: Horizontal(g5)
    c: DistanceX(g1,g1) = 1.63
    c: DistanceY(g0,g0) = 1.91
    c: DistanceY(g2,g2) = 0.8
    c: DistanceX(g5,g5) = 0.8
    c: Horizontal(g6)
    c: Coincident(g6,g7)
    c: Vertical(g7)
    c: Coincident(g7,g8)
    c: Horizontal(g8)
    c: Coincident(g8,g9)
    c: Vertical(g9)
    c: Coincident(g9,g10)
    c: Horizontal(g10)
    c: Coincident(g10,g11)
    c: Coincident(g11,g6)
    c: Vertical(g11)
    c: Equal(g6,g1)
    c: Equal(g7,g0)
    c: Equal(g8,g5)
    c: Equal(g11,g2)
    c: Vertical(g12)
    c: Coincident(g12,g13)
    c: Horizontal(g13)
    c: Coincident(g13,g14)
    c: Vertical(g14)
    c: Coincident(g14,g15)
    c: Horizontal(g15)
    c: Coincident(g15,g16)
    c: Vertical(g16)
    c: Coincident(g16,g17)
    c: Horizontal(g17)
    c: Vertical(g18)
    c: Coincident(g18,g19)
    c: Horizontal(g19)
    c: Coincident(g19,g20)
    c: Vertical(g20)
    c: Coincident(g20,g21)
    c: Horizontal(g21)
    c: Coincident(g21,g22)
    c: Vertical(g22)
    c: Coincident(g22,g23)
    c: Coincident(g23,g18)
    c: Horizontal(g23)
    c: Equal(g23,g8)
    c: Equal(g17,g5)
    c: Equal(g14,g20)
    c: Equal(g14,g2)
    c: Equal(g12,g22)
    c: Equal(g21,g13)
    c: Equal(g12,g0)
    c: Equal(g13,g1)
    c: Coincident(g-3,g0)
    c: Coincident(g-4,g6)
    c: Coincident(g-5,g12)
    c: Coincident(g-6,g21)
    c: Coincident(g17,g12)
FEATURE [PartDesign::Pad] Pad003
  BaseFeature = -> Chamfer
  Length = 3
  Length2 = 100
  Placement = pos=(0,0,0) rot=(1,0,0;1.5708rad)
  Profile = -> Sketch015
  Type = 0
FEATURE [Sketcher::SketchObject] Sketch007
  ExternalGeometry = -> [Chamfer]
  MapMode = 5
  Placement = pos=(0,0,0) rot=(-1,0,0;1.5708rad)
  Support = -> [Pad003]
  sketch-geometry (24):
    g0: LineSegment StartX=-9.2875 StartY=6.225 StartZ=0 EndX=-3.2875 EndY=6.225 EndZ=0
    g1: LineSegment StartX=-3.2875 StartY=6.225 StartZ=0 EndX=-3.2875 EndY=3.225 EndZ=0
    g2: LineSegment StartX=-3.2875 StartY=3.225 StartZ=0 EndX=-9.2875 EndY=3.225 EndZ=0
    g3: LineSegment StartX=-9.2875 StartY=3.225 StartZ=0 EndX=-9.2875 EndY=6.225 EndZ=0
    g4: LineSegment [constr] StartX=-12.575 StartY=6.225 StartZ=0 EndX=12.575 EndY=6.225 EndZ=0
    g5: LineSegment [constr] StartX=-12.575 StartY=-6.225 StartZ=0 EndX=12.575 EndY=-6.225 EndZ=0
    g6: GeomPoint X=1e-16 Y=6.225 Z=0
    g7: GeomPoint X=4e-16 Y=-6.225 Z=0
    g8: GeomPoint X=-6.2875 Y=-6.225 Z=0
    g9: GeomPoint X=6.2875 Y=-6.225 Z=0
    g10: GeomPoint X=-6.2875 Y=6.225 Z=0
    g11: GeomPoint X=6.2875 Y=6.225 Z=0
    g12: LineSegment StartX=3.2875 StartY=6.225 StartZ=0 EndX=9.2875 EndY=6.225 EndZ=0
    g13: LineSegment StartX=9.2875 StartY=6.225 StartZ=0 EndX=9.2875 EndY=3.225 EndZ=0
    g14: LineSegment StartX=9.2875 StartY=3.225 StartZ=0 EndX=3.2875 EndY=3.225 EndZ=0
    g15: LineSegment StartX=3.2875 StartY=3.225 StartZ=0 EndX=3.2875 EndY=6.225 EndZ=0
    g16: LineSegment StartX=-9.2875 StartY=-3.225 StartZ=0 EndX=-3.2875 EndY=-3.225 EndZ=0
    g17: LineSegment StartX=-3.2875 StartY=-3.225 StartZ=0 EndX=-3.2875 EndY=-6.225 EndZ=0
    g18: LineSegment StartX=-3.2875 StartY=-6.225 StartZ=0 EndX=-9.2875 EndY=-6.225 EndZ=0
    g19: LineSegment StartX=-9.2875 StartY=-6.225 StartZ=0 EndX=-9.2875 EndY=-3.225 EndZ=0
    g20: LineSegment StartX=3.2875 StartY=-3.225 StartZ=0 EndX=9.2875 EndY=-3.225 EndZ=0
    g21: LineSegment StartX=9.2875 StartY=-3.225 StartZ=0 EndX=9.2875 EndY=-6.225 EndZ=0
    g22: LineSegment StartX=9.2875 StartY=-6.225 StartZ=0 EndX=3.2875 EndY=-6.225 EndZ=0
    g23: LineSegment StartX=3.2875 StartY=-6.225 StartZ=0 EndX=3.2875 EndY=-3.225 EndZ=0
  constraints (54):
    c: Coincident(g0,g1)
    c: Coincident(g1,g2)
    c: Coincident(g2,g3)
    c: Coincident(g3,g0)
    c: Horizontal(g0)
    c: Horizontal(g2)
    c: Vertical(g1)
    c: Vertical(g3)
    c: DistanceX(g0,g0) = 6
    c: DistanceY(g1,g1) = 3
    c: Coincident(g4,g-3)
    c: Coincident(g4,g-4)
    c: Coincident(g5,g-6)
    c: Coincident(g5,g-5)
    c: Symmetric(g4,g4,g6)
    c: Symmetric(g5,g5,g7)
    c: Symmetric(g7,g5,g9)
    c: Symmetric(g5,g7,g8)
    c: Symmetric(g4,g6,g10)
    c: Symmetric(g6,g4,g11)
    c: Symmetric(g0,g0,g10)
    c: Coincident(g12,g13)
    c: Coincident(g13,g14)
    c: Coincident(g14,g15)
    c: Coincident(g15,g12)
    c: Horizontal(g12)
    c: Horizontal(g14)
    c: Vertical(g13)
    c: Vertical(g15)
    c: Coincident(g16,g17)
    c: Coincident(g17,g18)
    c: Coincident(g18,g19)
    c: Coincident(g19,g16)
    c: Horizontal(g16)
    c: Horizontal(g18)
    c: Vertical(g17)
    c: Vertical(g19)
    c: Coincident(g20,g21)
    c: Coincident(g21,g22)
    c: Coincident(g22,g23)
    c: Coincident(g23,g20)
    c: Horizontal(g20)
    c: Horizontal(g22)
    c: Vertical(g21)
    c: Vertical(g23)
    c: Equal(g12,g0)
    c: Equal(g20,g16)
    c: Equal(g16,g0)
    c: Equal(g17,g21)
    c: Equal(g21,g13)
    c: Equal(g13,g1)
    c: Symmetric(g18,g17,g8)
    c: Symmetric(g22,g21,g9)
    c: Symmetric(g12,g12,g11)
FEATURE [PartDesign::Pad] Pad004
  BaseFeature = -> Pad003
  Length = 2.6
  Length2 = 100
  Placement = pos=(0,0,0) rot=(1,0,0;1.5708rad)
  Profile = -> Sketch007
  Type = 0
FEATURE [Sketcher::SketchObject] Sketch008
  MapMode = 5
  Placement = pos=(0,0,0) rot=(-1,0,0;1.5708rad)
  Support = -> [Pad004]
  sketch-geometry (1):
    g0: Circle CenterX=0 CenterY=0 CenterZ=0 NormalX=0 NormalY=0 NormalZ=1 AngleXU=0 Radius=1.5
  constraints (2):
    c: Coincident(g0,g-1)
    c: Diameter(g0) = 3
FEATURE [Sketcher::SketchObject] Sketch016  label="SketchLeftBtn"
  MapMode = 5
  Placement = pos=(0,-4.5,3.4e-15) rot=(1,0,0;1.5708rad)
  Support = -> [DatumPlane]
  sketch-geometry (5):
    g0: LineSegment StartX=-11 StartY=4.65 StartZ=0 EndX=-1.7 EndY=4.65 EndZ=0
    g1: LineSegment StartX=-1.7 StartY=4.65 StartZ=0 EndX=-1.7 EndY=-4.65 EndZ=0
    g2: LineSegment StartX=-1.7 StartY=-4.65 StartZ=0 EndX=-11 EndY=-4.65 EndZ=0
    g3: LineSegment StartX=-11 StartY=-4.65 StartZ=0 EndX=-11 EndY=4.65 EndZ=0
    g4: LineSegment [constr] StartX=-6.35 StartY=4.65 StartZ=0 EndX=-6.35 EndY=-4.65 EndZ=0
  constraints (14):
    c: Coincident(g0,g1)
    c: Coincident(g1,g2)
    c: Coincident(g2,g3)
    c: Coincident(g3,g0)
    c: Horizontal(g0)
    c: Horizontal(g2)
    c: Vertical(g1)
    c: DistanceY(g3,g3) = 9.3
    c: DistanceX(g0,g0) = 9.3
    c: Symmetric(g0,g2,g-1)
    c: PointOnObject(g4,g0)
    c: PointOnObject(g4,g2)
    c: Symmetric(g0,g0,g4)
    c: DistanceX(g4,g-1) = 6.35
FEATURE [PartDesign::Pad] Pad006
  Length = 1.8
  Length2 = 100
  Placement = pos=(0,-4.5,5e-15) rot=(1,0,0;1.5708rad)
  Profile = -> Sketch016
  Type = 0
FEATURE [PartDesign::Chamfer] Chamfer001  label="BtnLeftChamfer"
  Base = -> Pad006 [Face6]
  BaseFeature = -> Pad006
  Placement = pos=(0,-4.5,5e-15) rot=(1,0,0;1.5708rad)
  Size = 0.35
FEATURE [PartDesign::Body] Body001  label="ButtonLeftBody"
  Group = -> [Sketch016,Pad006,Chamfer001]
  Origin = -> Origin001
  Tip = -> Chamfer001
FEATURE [PartDesign::Chamfer] Chamfer002  label="BtnRightChamfer"
  Base = -> Pad002 [Face6]
  BaseFeature = -> Pad002
  Placement = pos=(0,-4.5,5e-15) rot=(1,0,0;1.5708rad)
  Size = 0.35
FEATURE [PartDesign::Body] Body002  label="ButtonRightBody"
  Group = -> [Sketch011,Pad002,Chamfer002]
  Origin = -> Origin002
  Tip = -> Chamfer002
FEATURE [Part::Feature] Part__Feature  label="COMMON-Brass_pin-5.75mm"
  Placement = pos=(20.32,0,0) rot=(0,0,1;0rad)
  shape: bbox 0.7 x 5.75 x 0.7 mm, 14 faces (baked)
FEATURE [PartDesign::Body] Body003  label="PCBBody"
  Group = -> [Sketch012,Pad008]
  Origin = -> Origin003
  Tip = -> Pad008
FEATURE [Part::Feature] Part__Feature002  label="BTN_B-Brass_pin-5.75mm"
  shape: bbox 0.7 x 5.75 x 0.7 mm, 14 faces (baked)
FEATURE [PartDesign::Pad] Pad005
  BaseFeature = -> Pad004
  Length = 2
  Length2 = 100
  Placement = pos=(0,0,0) rot=(1,0,0;1.5708rad)
  Profile = -> Sketch008
  Type = 0
FEATURE [PartDesign::Fillet] Fillet004
  Base = -> Pad005 [Edge179]
  BaseFeature = -> Pad005
  Placement = pos=(0,0,0) rot=(1,0,0;1.5708rad)
  Radius = 0.5
FEATURE [PartDesign::Chamfer] Chamfer003
  Base = -> Fillet004 [Edge146,Edge147,Edge130,Edge129]
  BaseFeature = -> Fillet004
  Placement = pos=(0,0,0) rot=(1,0,0;1.5708rad)
  Size = 1.3
FEATURE [Sketcher::SketchObject] Sketch017
  MapMode = 5
  Support = -> [XY_Plane004]
  sketch-geometry (8):
    g0: LineSegment StartX=-10.375 StartY=5.5 StartZ=0 EndX=10.375 EndY=5.5 EndZ=0
    g1: LineSegment StartX=11.375 StartY=4.5 StartZ=0 EndX=11.375 EndY=1 EndZ=0
    g2: LineSegment StartX=10.375 StartY=0 StartZ=0 EndX=-10.375 EndY=0 EndZ=0
    g3: LineSegment StartX=-11.375 StartY=1 StartZ=0 EndX=-11.375 EndY=4.5 EndZ=0
    g4: ArcOfCircle CenterX=-10.375 CenterY=4.5 CenterZ=0 NormalX=0 NormalY=0 NormalZ=1 AngleXU=0 Radius=1 StartAngle=1.5708 EndAngle=3.14159
    g5: ArcOfCircle CenterX=10.375 CenterY=4.5 CenterZ=0 NormalX=0 NormalY=0 NormalZ=1 AngleXU=0 Radius=1 StartAngle=0 EndAngle=1.5708
    g6: ArcOfCircle CenterX=10.375 CenterY=1 CenterZ=0 NormalX=0 NormalY=0 NormalZ=1 AngleXU=0 Radius=1 StartAngle=4.71239 EndAngle=6.28319
    g7: ArcOfCircle CenterX=-10.375 CenterY=1 CenterZ=0 NormalX=0 NormalY=0 NormalZ=1 AngleXU=0 Radius=1 StartAngle=3.14159 EndAngle=4.71239
  constraints (19):
    c: Horizontal(g2)
    c: Vertical(g1)
    c: Vertical(g3)
    c: Tangent(g3,g4) = 1.5708
    c: Tangent(g0,g4) = 1.5708
    c: Tangent(g0,g5) = 1.5708
    c: Tangent(g1,g5) = 1.5708
    c: Tangent(g1,g6) = 1.5708
    c: Tangent(g2,g6) = 1.5708
    c: Tangent(g2,g7) = 1.5708
    c: Tangent(g3,g7) = 1.5708
    c: Radius(g4) = 1
    c: Equal(g5,g6)
    c: Equal(g6,g7)
    c: Equal(g7,g4)
    c: Symmetric(g0,g0,g-2)
    c: PointOnObject(g-1,g2)
    c: DistanceY(g-1,g0) = 5.5
    c: DistanceX(g3,g1) = 22.75
FEATURE [PartDesign::Pad] Pad007  label="LabelPad"
  Length = 0.05
  Length2 = 100
  Profile = -> Sketch017
  Type = 0
FEATURE [PartDesign::FeatureBase] BaseFeature
  BaseFeature = -> Pad007
FEATURE [PartDesign::Body] Body004  label="LabelBody"
  BaseFeature = -> Pad007
  Group = -> [BaseFeature]
  Origin = -> Origin004
  Placement = pos=(0,0,6.2) rot=(0,0,1;3.14159rad)
  Tip = -> BaseFeature
FEATURE [Part::Part2DObjectPython] ShapeString  label="LabelTextShapeString"  # Draft 2D object (typed FeaturePython)
  AttachmentOffset = pos=(-6.75,2.8,0.01) rot=(0,0,1;0rad)
  FontFile = <path>
  MapMode = 5
  Placement = pos=(-6.75,2.8,0.06) rot=(0,0,1;0rad)
  Size = 1
  String = 87DC3-201
  Support = -> [Pad007]
  Tracking = 0.05
FEATURE [Part::Extrusion] Extrude  label="LabelTextExtrude"
  Base = -> ShapeString
  Dir = (0,0,1)
  DirMode = 2
  FaceMakerClass = Part::FaceMakerBullseye
  LengthFwd = 0.05
  LengthRev = 0
  Placement = pos=(0,0,6.2) rot=(0,0,1;3.14159rad)
  Solid = true
  Symmetric = false
FEATURE [PartDesign::Fillet] Fillet005
  Base = -> Chamfer003 [Edge10,Edge151,Edge156,Edge158]
  BaseFeature = -> Chamfer003
  Placement = pos=(0,0,0) rot=(1,0,0;1.5708rad)
  Radius = 1.5
FEATURE [PartDesign::Fillet] Fillet003
  Base = -> Fillet005 [Edge164,Edge165,Edge145,Edge9]
  BaseFeature = -> Fillet005
  Placement = pos=(0,0,0) rot=(1,0,0;1.5708rad)
  Radius = 1
FEATURE [Sketcher::SketchObject] Sketch009
  ExternalGeometry = -> [Fillet003]
  MapMode = 5
  Placement = pos=(0,5.2e-15,3.225) rot=(1,0,0;3.14159rad)
  Support = -> [Fillet003]
  sketch-geometry (4):
    g0: LineSegment StartX=-9.2875 StartY=2e-16 StartZ=0 EndX=-3.2875 EndY=2e-16 EndZ=0
    g1: LineSegment StartX=-3.2875 StartY=2e-16 StartZ=0 EndX=-3.2875 EndY=-1.6 EndZ=0
    g2: LineSegment StartX=-3.2875 StartY=-1.6 StartZ=0 EndX=-9.2875 EndY=-1.6 EndZ=0
    g3: LineSegment StartX=-9.2875 StartY=-1.6 StartZ=0 EndX=-9.2875 EndY=2e-16 EndZ=0
  constraints (10):
    c: Coincident(g0,g1)
    c: Coincident(g1,g2)
    c: Coincident(g2,g3)
    c: Coincident(g3,g0)
    c: Vertical(g1)
    c: Coincident(g0,g-3)
    c: DistanceY(g1,g1) = 1.6
    c: Equal(g3,g1)
    c: Equal(g2,g0)
    c: Coincident(g0,g-4)
FEATURE [PartDesign::Pocket] Pocket006
  BaseFeature = -> Fillet003
  Length = 1.8
  Length2 = 100
  Placement = pos=(0,0,0) rot=(1,0,0;1.5708rad)
  Profile = -> Sketch009
  Type = 0
FEATURE [Sketcher::SketchObject] Sketch010
  ExternalGeometry = -> [Pocket006]
  MapMode = 5
  Placement = pos=(0,5.2e-15,3.225) rot=(1,0,0;3.14159rad)
  Support = -> [Pocket006]
  sketch-geometry (4):
    g0: LineSegment StartX=3.2875 StartY=0 StartZ=0 EndX=9.2875 EndY=2e-16 EndZ=0
    g1: LineSegment StartX=9.2875 StartY=2e-16 StartZ=0 EndX=9.2875 EndY=-1.6 EndZ=0
    g2: LineSegment StartX=9.2875 StartY=-1.6 StartZ=0 EndX=3.2875 EndY=-1.6 EndZ=0
    g3: LineSegment StartX=3.2875 StartY=-1.6 StartZ=0 EndX=3.2875 EndY=0 EndZ=0
  constraints (10):
    c: Coincident(g0,g1)
    c: Coincident(g1,g2)
    c: Coincident(g2,g3)
    c: Coincident(g3,g0)
    c: Horizontal(g2)
    c: Vertical(g1)
    c: Vertical(g3)
    c: Coincident(g0,g-3)
    c: Coincident(g0,g-4)
    c: DistanceY(g1,g1) = 1.6
FEATURE [PartDesign::Pocket] Pocket007
  BaseFeature = -> Pocket006
  Length = 1.8
  Length2 = 100
  Placement = pos=(0,0,0) rot=(1,0,0;1.5708rad)
  Profile = -> Sketch010
  Type = 0
FEATURE [PartDesign::Plane] DatumPlane001
  Length = 24.4855
  MapMode = 45
  Placement = pos=(-1.37e-14,1.3,-3.225) rot=(0,0,1;1.5708rad)
  ResizeMode = 0
  Support = -> [Pocket007]
  Width = 29.6355
FEATURE [Sketcher::SketchObject] Sketch014
  ExternalGeometry = -> [Pocket007]
  MapMode = 5
  Placement = pos=(-1.37e-14,1.3,-3.225) rot=(0,0,1;1.5708rad)
  Support = -> [DatumPlane001]
  sketch-geometry (8):
    g0: LineSegment StartX=-1.3 StartY=9.2875 StartZ=0 EndX=0.3 EndY=9.2875 EndZ=0
    g1: LineSegment StartX=0.3 StartY=9.2875 StartZ=0 EndX=0.3 EndY=3.2875 EndZ=0
    g2: LineSegment StartX=0.3 StartY=3.2875 StartZ=0 EndX=-1.3 EndY=3.2875 EndZ=0
    g3: LineSegment StartX=-1.3 StartY=3.2875 StartZ=0 EndX=-1.3 EndY=9.2875 EndZ=0
    g4: LineSegment StartX=-1.3 StartY=-3.2875 StartZ=0 EndX=0.3 EndY=-3.2875 EndZ=0
    g5: LineSegment StartX=0.3 StartY=-3.2875 StartZ=0 EndX=0.3 EndY=-9.2875 EndZ=0
    g6: LineSegment StartX=0.3 StartY=-9.2875 StartZ=0 EndX=-1.3 EndY=-9.2875 EndZ=0
    g7: LineSegment StartX=-1.3 StartY=-9.2875 StartZ=0 EndX=-1.3 EndY=-3.2875 EndZ=0
  constraints (20):
    c: Coincident(g0,g1)
    c: Coincident(g1,g2)
    c: Coincident(g2,g3)
    c: Coincident(g3,g0)
    c: Horizontal(g0)
    c: Horizontal(g2)
    c: Vertical(g1)
    c: Coincident(g0,g-3)
    c: Coincident(g4,g5)
    c: Coincident(g5,g6)
    c: Coincident(g6,g7)
    c: Coincident(g7,g4)
    c: Horizontal(g4)
    c: Horizontal(g6)
    c: Vertical(g5)
    c: Coincident(g4,g-5)
    c: Coincident(g2,g-4)
    c: Coincident(g6,g-6)
    c: DistanceX(g4,g4) = 1.6
    c: Equal(g4,g2)
FEATURE [PartDesign::Pocket] Pocket005  label="BodyFinal_pad"
  BaseFeature = -> Pocket007
  Length = 1.8
  Length2 = 100
  Placement = pos=(0,0,0) rot=(1,0,0;1.5708rad)
  Profile = -> Sketch014
  Type = 0
FEATURE [PartDesign::Body] Body005  label="87DC3-201Body"
  Group = -> [Sketch013,Pad001,Sketch018,Pocket008,Chamfer,DatumPlane,Sketch015,Pad003,Sketch007,Pad004,Sketch008,Pad005,Fillet004,Chamfer003,Fillet005,Fillet003,Sketch009,Pocket006,Sketch010,Pocket007,DatumPlane001,Sketch014,Pocket005]
  Origin = -> Origin006
  Tip = -> Pocket005
FEATURE [Part::Compound] Compound  label="Compound_Grayhill_87DC3-201"
  Links = -> [Body005,Body002,Body004,Body001,Pad007,Part__Feature001,Part__Feature,Body003,Part__Feature002,Extrude]
  Placement = pos=(0,-22,1.4) rot=(1,0,0;1.5708rad)
FEATURE [Part::Feature] Part__Feature003  label="Body001"
  shape: bbox 26.3 x 19 x 28.2 mm, 42 faces (baked)
FEATURE [Part::Feature] Part__Feature004  label="M8x7.0-ScrewTap001"
  shape: bbox 10.62 x 11.9 x 10 mm, 30 faces (baked)
FEATURE [Part::Compound] Compound001  label="Compound_KY040_RotaryEncoder"
  Links = -> [Part__Feature003,Part__Feature004]
  Placement = pos=(0,0,10.6) rot=(1,0,0;3.14159rad)
FEATURE [Part::FeaturePython] Screw  label="M3x10-Screw"  # Fasteners workbench fastener (typed FeaturePython)
  Placement = pos=(-11,-12.5,-1.2) rot=(0,1,0;3.14159rad)
  diameter = 4
  invert = false
  length = 3
  lengthCustom = 10
  matchOuter = false
  offset = 0
  thread = false
  type = 11
FEATURE [Part::FeaturePython] Screw001  label="M3x10-Screw001"  # Fasteners workbench fastener (typed FeaturePython)
  Placement = pos=(11,-12.5,-1.2) rot=(0,1,0;3.14159rad)
  diameter = 4
  invert = false
  length = 3
  lengthCustom = 10
  matchOuter = false
  offset = 0
  thread = false
  type = 11
FEATURE [Part::FeaturePython] Nut  label="M3-Nut"  # Fasteners workbench fastener (typed FeaturePython)
  Placement = pos=(-11,-12.5,6.1) rot=(0,0,1;0.523599rad)
  diameter = 4
  invert = false
  matchOuter = false
  offset = 0
  thread = false
  type = 6
FEATURE [Part::FeaturePython] Nut001  label="M3-Nut001"  # Fasteners workbench fastener (typed FeaturePython)
  Placement = pos=(11,-12.5,6.1) rot=(0,0,1;0.523599rad)
  diameter = 4
  invert = false
  matchOuter = false
  offset = 0
  thread = false
  type = 6
FEATURE [Part::FeaturePython] Screw002  label="M2.5x16-Screw"  # Fasteners workbench fastener (typed FeaturePython)
  Placement = pos=(-6,8.5,-1.2) rot=(0,1,0;3.14159rad)
  diameter = 3
  invert = false
  length = 7
  lengthCustom = 16
  matchOuter = false
  offset = 0
  thread = false
  type = 11
FEATURE [Part::FeaturePython] Screw003  label="M2.5x16-Screw001"  # Fasteners workbench fastener (typed FeaturePython)
  Placement = pos=(8,8.5,-1.2) rot=(0,1,0;3.14159rad)
  diameter = 3
  invert = false
  length = 7
  lengthCustom = 16
  matchOuter = false
  offset = 0
  thread = false
  type = 11
FEATURE [Part::FeaturePython] Nut002  label="M2.5-Nut"  # Fasteners workbench fastener (typed FeaturePython)
  Placement = pos=(-6,8.5,10.6) rot=(0,0,1;0rad)
  diameter = 3
  invert = false
  matchOuter = false
  offset = 0
  thread = false
  type = 6
FEATURE [Part::FeaturePython] Nut003  label="M2.5-Nut001"  # Fasteners workbench fastener (typed FeaturePython)
  Placement = pos=(8,8.5,10.6) rot=(0,0,1;0rad)
  diameter = 3
  invert = false
  matchOuter = false
  offset = 0
  thread = false
  type = 6
FEATURE [App::DocumentObjectGroup] Group  label="3d_holder_right-asm_group"
  Group = -> [Body,Compound,Compound001,Screw,Screw001,Nut,Nut001,Screw002,Screw003,Nut002,Nut003]
FEATURE [Part::Feature] Part__Feature005  label="PinHeader_1x03_P254mm_Vertical"
  Placement = pos=(0,-30.89,0) rot=(0,0,1;1.5708rad)
  shape: bbox 7.62 x 2.54 x 11.54 mm, 76 faces (baked)
FEATURE [Part::Feature] Part__Feature006  label="PinSocket_1x05_P254mm_Vertical"
  Placement = pos=(13,5.08,9.4) rot=(0,1,0;3.14159rad)
  shape: bbox 2.54 x 12.7 x 10.1 mm, 165 faces (baked)
FEATURE [Part::Feature] Part__Feature007  label="PinHeader_1x05_P254mm_Vertical"
  Placement = pos=(13,5.08,0) rot=(0,0,1;0rad)
  shape: bbox 2.54 x 12.7 x 11.54 mm, 124 faces (baked)
FEATURE [App::DocumentObjectGroup] Group001  label="Rotary_connector_9.4mm"
  Group = -> [Part__Feature007,Part__Feature006]
note: 1 file-system path scrubbed to <path> (originals preserved in the JSON sidecar)
